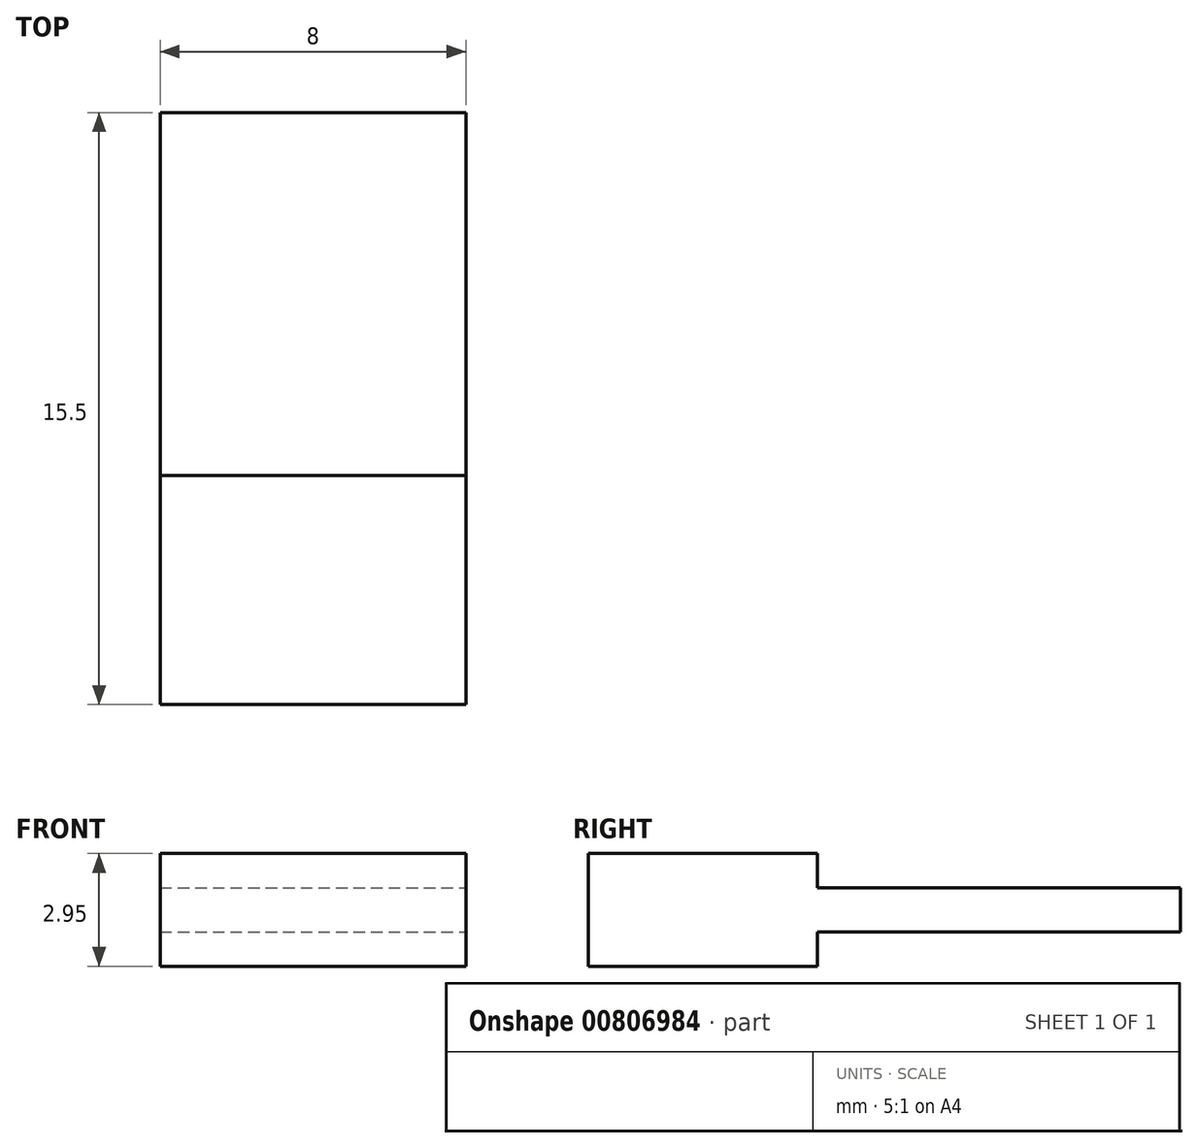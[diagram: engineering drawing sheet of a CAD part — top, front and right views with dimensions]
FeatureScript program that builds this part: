
annotation { "Feature Type Name" : "Feature", "Feature Type Description" : "" }
export const myFeature = defineFeature(function(context is Context, id is Id, definition is map)
    precondition{}
    {
        {
            var Q0;
            Q0=qCreatedBy(makeId("Top.planeOp"),FACE);
            var sketch = newSketch(context, id + "F0", { "sketchPlane" : qUnion([Q0])});
            skLineSegment(sketch, "E0.bottom", {"start": v(-4, 15.5) * mm, "end": v(4, 15.5) * mm});
            skLineSegment(sketch, "E0.top", {"start": v(-4, 0) * mm, "end": v(4, 0) * mm});
            skLineSegment(sketch, "E0.left", {"start": v(-4, 15.5) * mm, "end": v(-4, 0) * mm});
            skLineSegment(sketch, "E0.right", {"start": v(4, 15.5) * mm, "end": v(4, 0) * mm});
            skSolve(sketch);
        }
        {
            var Q0;
            Q0=makeQuery(id+"F0.imprint","IMPRINT",FACE,{"disambiguationData":[TD([[makeQuery(id+"F0.imprint","IMPRINT",EDGE,{"derivedFrom":sQuery(id+"F0.wireOp",EDGE,"E0.bottom")}),-1.0]])]});
            extrude(context, id + "F1", {"entities" : qUnion([Q0]), "depth" : 2.95 * mm, "offsetDistance" : 25 * mm});
        }
        {
            var Q0;
            Q0=makeQuery(id+"F1.opExtrude","CAP_FACE",FACE,{"disambiguationData":[OSD([sQuery(id+"F0.wireOp",EDGE,"E0.bottom"),sQuery(id+"F0.wireOp",EDGE,"E0.top"),sQuery(id+"F0.wireOp",EDGE,"E0.left"),sQuery(id+"F0.wireOp",EDGE,"E0.right")])],"isStart":false});
            var sketch = newSketch(context, id + "F2", { "sketchPlane" : qUnion([Q0])});
            skLineSegment(sketch, "E1.bottom", {"start": v(-4, 15.5) * mm, "end": v(4, 15.5) * mm});
            skLineSegment(sketch, "E1.top", {"start": v(-4, 6) * mm, "end": v(4, 6) * mm});
            skLineSegment(sketch, "E1.left", {"start": v(-4, 15.5) * mm, "end": v(-4, 6) * mm});
            skLineSegment(sketch, "E1.right", {"start": v(4, 15.5) * mm, "end": v(4, 6) * mm});
            skSolve(sketch);
        }
        {
            var Q0;
            Q0=makeQuery(id+"F2.imprint","IMPRINT",FACE,{"disambiguationData":[TD([[makeQuery(id+"F2.imprint","IMPRINT",EDGE,{"derivedFrom":sQuery(id+"F2.wireOp",EDGE,"E1.bottom")}),-1.0]])]});
            extrude(context, id + "F3", {"entities" : qUnion([Q0]), "operationType" : NewBodyOperationType.REMOVE, "oppositeDirection" : true, "depth" : .9 * mm, "offsetDistance" : 25 * mm});
        }
        {
            var Q0;
            Q0=makeQuery(id+"F1.opExtrude","CAP_FACE",FACE,{"disambiguationData":[OSD([sQuery(id+"F0.wireOp",EDGE,"E0.bottom"),sQuery(id+"F0.wireOp",EDGE,"E0.top"),sQuery(id+"F0.wireOp",EDGE,"E0.left"),sQuery(id+"F0.wireOp",EDGE,"E0.right")])],"isStart":true});
            var sketch = newSketch(context, id + "F4", { "sketchPlane" : qUnion([Q0])});
            skLineSegment(sketch, "E2.bottom", {"start": v(4, -15.5) * mm, "end": v(-4, -15.5) * mm});
            skLineSegment(sketch, "E2.top", {"start": v(4, -6) * mm, "end": v(-4, -6) * mm});
            skLineSegment(sketch, "E2.left", {"start": v(4, -15.5) * mm, "end": v(4, -6) * mm});
            skLineSegment(sketch, "E2.right", {"start": v(-4, -15.5) * mm, "end": v(-4, -6) * mm});
            skSolve(sketch);
        }
        {
            var Q0;
            Q0=makeQuery(id+"F4.imprint","IMPRINT",FACE,{"disambiguationData":[TD([[makeQuery(id+"F4.imprint","IMPRINT",EDGE,{"derivedFrom":sQuery(id+"F4.wireOp",EDGE,"E2.bottom")}),1.0]])]});
            extrude(context, id + "F5", {"entities" : qUnion([Q0]), "operationType" : NewBodyOperationType.REMOVE, "oppositeDirection" : true, "depth" : .9 * mm, "offsetDistance" : 25 * mm});
        }
    });
